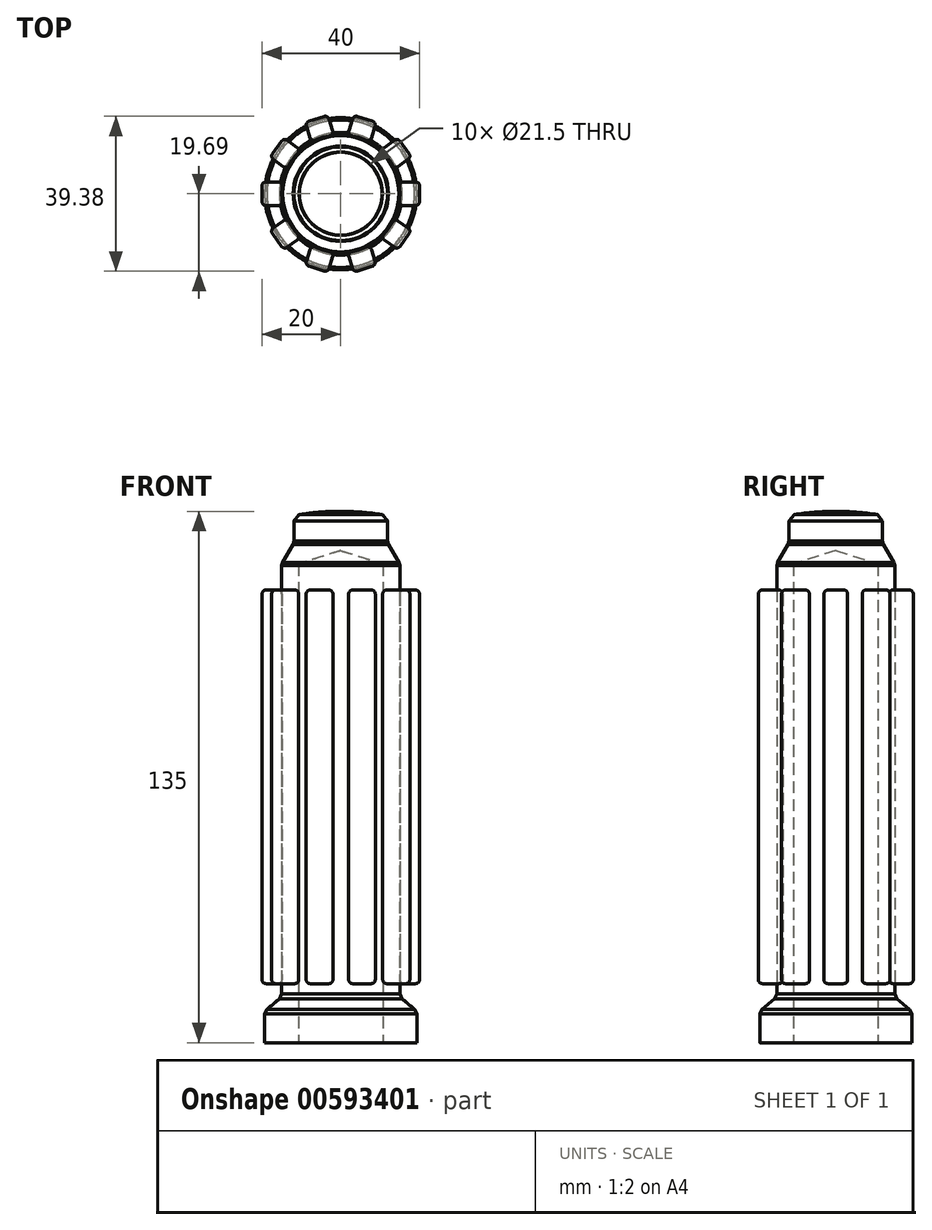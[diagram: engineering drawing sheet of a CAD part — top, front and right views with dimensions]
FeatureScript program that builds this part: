
annotation { "Feature Type Name" : "Feature", "Feature Type Description" : "" }
export const myFeature = defineFeature(function(context is Context, id is Id, definition is map)
    precondition{}
    {
        {
            var Q0;
            Q0=qCreatedBy(makeId("Front.planeOp"),FACE);
            var sketch = newSketch(context, id + "F0", { "sketchPlane" : qUnion([Q0])});
            skLineSegment(sketch, "E0", {"start": v(10.75, 121.63) * mm, "end": v(10.75, 0) * mm});
            skLineSegment(sketch, "E1", {"start": v(10.75, 0) * mm, "end": v(19.33, 0) * mm});
            skLineSegment(sketch, "E2", {"start": v(19.32, 0) * mm, "end": v(19.32, 8) * mm});
            skLineSegment(sketch, "E3", {"start": v(19.32, 8) * mm, "end": v(15, 11.63) * mm});
            skLineSegment(sketch, "E4", {"start": v(15, 11.63) * mm, "end": v(15, 121.63) * mm});
            skLineSegment(sketch, "E5", {"start": v(15, 121.63) * mm, "end": v(11.9, 127) * mm});
            skLineSegment(sketch, "E6", {"start": v(0, 125) * mm, "end": v(0, 135) * mm});
            skLineSegment(sketch, "E7", {"start": v(11.9, 127) * mm, "end": v(11.9, 133.95) * mm});
            skLineSegment(sketch, "E8", {"start": v(0, 0) * mm, "end": v(0, 135) * mm, "construction": true});
            skLineSegment(sketch, "E9", {"start": v(0, 125) * mm, "end": v(10.75, 121.63) * mm});
            skArc(sketch, "E10", {"start": v(11.9, 133.95) * mm, "mid": v(5.97, 134.74) * mm, "end": v(0, 135) * mm});
            skSolve(sketch);
        }
        {
            var Q0;
            Q0 = qSketchRegion(id + "F0", true);
            var Q1;
            Q1=sQuery(id+"F0.wireOp",EDGE,"E8");
            revolve(context, id + "F1", {"surfaceOperationType" : NewSurfaceOperationType.NEW, "entities" : qUnion([Q0]), "axis" : qUnion([Q1]), "revolveType" : RevolveType.FULL});
        }
        {
            var Q0;
            Q0=makeQuery(id+"F1.opRevolve","SWEPT_EDGE",EDGE,{"disambiguationData":[OSD([sQuery(id+"F0.wireOp",EDGE,"E7"),sQuery(id+"F0.wireOp",EDGE,"E10")])]});
            var Q1;
            Q1=makeQuery(id+"F1.opRevolve","SWEPT_EDGE",EDGE,{"disambiguationData":[OSD([sQuery(id+"F0.wireOp",EDGE,"E5"),sQuery(id+"F0.wireOp",EDGE,"E7")])]});
            var Q2;
            Q2=makeQuery(id+"F1.opRevolve","SWEPT_EDGE",EDGE,{"disambiguationData":[OSD([sQuery(id+"F0.wireOp",EDGE,"E4"),sQuery(id+"F0.wireOp",EDGE,"E5")])]});
            var Q3;
            Q3=makeQuery(id+"F1.opRevolve","SWEPT_EDGE",EDGE,{"disambiguationData":[OSD([sQuery(id+"F0.wireOp",EDGE,"E3"),sQuery(id+"F0.wireOp",EDGE,"E4")])]});
            var Q4;
            Q4=makeQuery(id+"F1.opRevolve","SWEPT_EDGE",EDGE,{"disambiguationData":[OSD([sQuery(id+"F0.wireOp",EDGE,"E2"),sQuery(id+"F0.wireOp",EDGE,"E3")])]});
            chamfer(context, id + "F2", {"entities" : qUnion([Q0, Q1, Q2, Q3, Q4]), "width" : 1.6 * mm, "tangentPropagation" : true});
        }
        {
            var Q0;
            Q0=qCreatedBy(makeId("Right.planeOp"),FACE);
            cPlane(context, id + "F3", {"entities" : qUnion([Q0]), "cplaneType" : CPlaneType.OFFSET, "offset" : 20 * mm, "width" : 150 * mm, "height" : 150 * mm});
        }
        {
            var Q0;
            Q0=qCreatedBy(id+"F3.planeOp",FACE);
            var sketch = newSketch(context, id + "F4", { "sketchPlane" : qUnion([Q0])});
            skLineSegment(sketch, "E11.bottom", {"start": v(-3, 15) * mm, "end": v(3, 15) * mm});
            skLineSegment(sketch, "E11.top", {"start": v(-3, 115) * mm, "end": v(3, 115) * mm});
            skLineSegment(sketch, "E11.left", {"start": v(-3, 15) * mm, "end": v(-3, 115) * mm});
            skLineSegment(sketch, "E11.right", {"start": v(3, 15) * mm, "end": v(3, 115) * mm});
            skSolve(sketch);
        }
        {
            var Q0;
            Q0 = qSketchRegion(id + "F4", true);
            var Q1;
            Q1=makeQuery(id+"F1.opRevolve","SWEPT_FACE",FACE,{"disambiguationData":[OSD([sQuery(id+"F0.wireOp",EDGE,"E4")])]});
            extrude(context, id + "F5", {"entities" : qUnion([Q0]), "endBound" : BoundingType.UP_TO_SURFACE, "oppositeDirection" : true, "depth" : 25 * mm, "endBoundEntityFace" : qUnion([Q1]), "offsetDistance" : 25 * mm});
        }
        {
            var Q0;
            Q0=makeQuery(id+"F5.opExtrude","CAP_EDGE",EDGE,{"disambiguationData":[OSD([sQuery(id+"F4.wireOp",EDGE,"E11.left")])],"isStart":true});
            var Q1;
            Q1=makeQuery(id+"F5.opExtrude","CAP_EDGE",EDGE,{"disambiguationData":[OSD([sQuery(id+"F4.wireOp",EDGE,"E11.right")])],"isStart":true});
            var Q2;
            Q2=makeQuery(id+"F5.opExtrude","CAP_EDGE",EDGE,{"disambiguationData":[OSD([sQuery(id+"F4.wireOp",EDGE,"E11.left")])],"isStart":false});
            var Q3;
            Q3=makeQuery(id+"F5.opExtrude","CAP_EDGE",EDGE,{"disambiguationData":[OSD([sQuery(id+"F4.wireOp",EDGE,"E11.right")])],"isStart":false});
            var Q4;
            Q4=makeQuery(id+"F5.opExtrude","CAP_EDGE",EDGE,{"disambiguationData":[OSD([sQuery(id+"F4.wireOp",EDGE,"E11.bottom")])],"isStart":false});
            var Q5;
            Q5=makeQuery(id+"F5.opExtrude","SWEPT_EDGE",EDGE,{"disambiguationData":[OSD([sQuery(id+"F4.wireOp",EDGE,"E11.bottom"),sQuery(id+"F4.wireOp",EDGE,"E11.left")])]});
            var Q6;
            Q6=makeQuery(id+"F5.opExtrude","SWEPT_EDGE",EDGE,{"disambiguationData":[OSD([sQuery(id+"F4.wireOp",EDGE,"E11.bottom"),sQuery(id+"F4.wireOp",EDGE,"E11.right")])]});
            var Q7;
            Q7=makeQuery(id+"F5.opExtrude","CAP_EDGE",EDGE,{"disambiguationData":[OSD([sQuery(id+"F4.wireOp",EDGE,"E11.bottom")])],"isStart":true});
            var Q8;
            Q8=makeQuery(id+"F5.opExtrude","SWEPT_EDGE",EDGE,{"disambiguationData":[OSD([sQuery(id+"F4.wireOp",EDGE,"E11.top"),sQuery(id+"F4.wireOp",EDGE,"E11.right")])]});
            var Q9;
            Q9=makeQuery(id+"F5.opExtrude","CAP_EDGE",EDGE,{"disambiguationData":[OSD([sQuery(id+"F4.wireOp",EDGE,"E11.top")])],"isStart":false});
            var Q10;
            Q10=makeQuery(id+"F5.opExtrude","SWEPT_EDGE",EDGE,{"disambiguationData":[OSD([sQuery(id+"F4.wireOp",EDGE,"E11.top"),sQuery(id+"F4.wireOp",EDGE,"E11.left")])]});
            var Q11;
            Q11=makeQuery(id+"F5.opExtrude","CAP_EDGE",EDGE,{"disambiguationData":[OSD([sQuery(id+"F4.wireOp",EDGE,"E11.top")])],"isStart":true});
            fillet(context, id + "F6", {"entities" : qUnion([Q0, Q1, Q2, Q3, Q4, Q5, Q6, Q7, Q8, Q9, Q10, Q11]), "radius" : 1 * mm, "tangentPropagation" : true, "allowEdgeOverflow" : false});
        }
        {
            var Q0;
            Q0=makeQuery(id+"F1.opRevolve","SWEPT_BODY",BODY,{"disambiguationData":[OSD([sQuery(id+"F0.wireOp",EDGE,"E0"),sQuery(id+"F0.wireOp",EDGE,"E1"),sQuery(id+"F0.wireOp",EDGE,"E2"),sQuery(id+"F0.wireOp",EDGE,"E3"),sQuery(id+"F0.wireOp",EDGE,"E4"),sQuery(id+"F0.wireOp",EDGE,"E5"),sQuery(id+"F0.wireOp",EDGE,"E6"),sQuery(id+"F0.wireOp",EDGE,"E7"),sQuery(id+"F0.wireOp",EDGE,"E9"),sQuery(id+"F0.wireOp",EDGE,"E10")])]});
            var Q1;
            Q1=makeQuery(id+"F5.opExtrude","SWEPT_BODY",BODY,{"disambiguationData":[OSD([sQuery(id+"F4.wireOp",EDGE,"E11.bottom"),sQuery(id+"F4.wireOp",EDGE,"E11.top"),sQuery(id+"F4.wireOp",EDGE,"E11.left"),sQuery(id+"F4.wireOp",EDGE,"E11.right")])]});
            var Q2;
            Q2=makeQuery(id+"F1.opRevolve","SWEPT_FACE",FACE,{"disambiguationData":[OSD([sQuery(id+"F0.wireOp",EDGE,"E4")])]});
            circularPattern(context, id + "F7", {"entities" : qUnion([Q0, Q1]), "axis" : qUnion([Q2]), "angle" : 360 * degree, "instanceCount" : 10, "equalSpace" : true});
        }
    });
